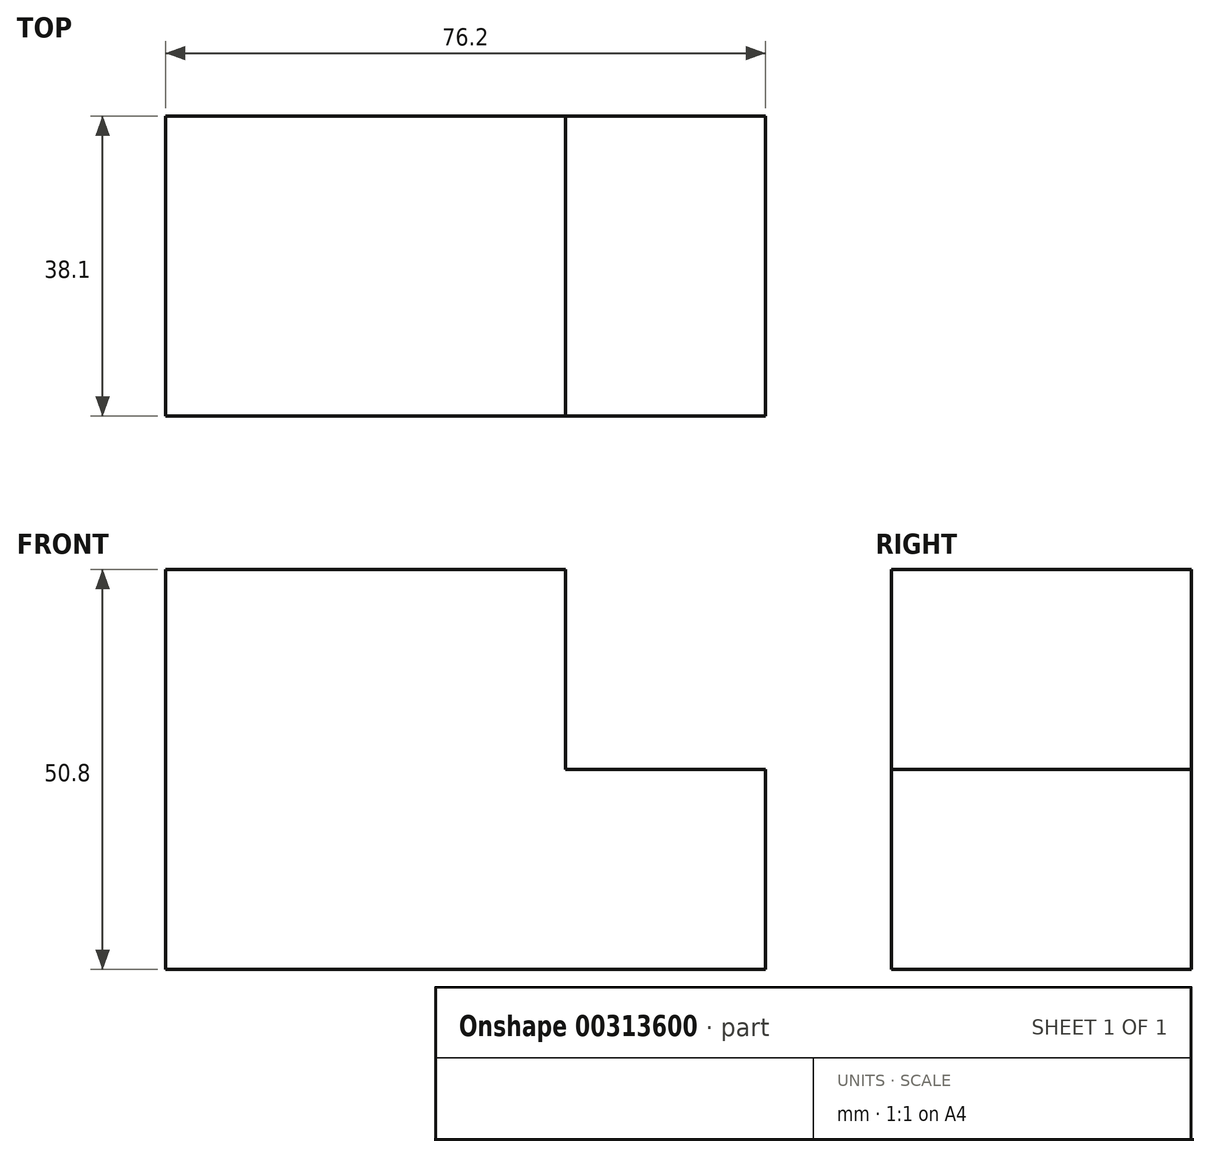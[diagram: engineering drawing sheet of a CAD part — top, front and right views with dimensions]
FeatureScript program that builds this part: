
annotation { "Feature Type Name" : "Feature", "Feature Type Description" : "" }
export const myFeature = defineFeature(function(context is Context, id is Id, definition is map)
    precondition{}
    {
        {
            var Q0;
            Q0=qCreatedBy(makeId("Front.planeOp"),FACE);
            var sketch = newSketch(context, id + "F0", { "sketchPlane" : qUnion([Q0])});
            skLineSegment(sketch, "E0", {"start": v(-38.24, -50.8) * mm, "end": v(37.96, -50.8) * mm});
            skLineSegment(sketch, "E1", {"start": v(37.96, -25.4) * mm, "end": v(12.56, -25.4) * mm});
            skLineSegment(sketch, "E2", {"start": v(12.56, -25.4) * mm, "end": v(12.56, 0) * mm});
            skLineSegment(sketch, "E3", {"start": v(12.56, 0) * mm, "end": v(-38.24, 0) * mm});
            skLineSegment(sketch, "E4", {"start": v(-38.24, 0) * mm, "end": v(-38.24, -50.8) * mm});
            skLineSegment(sketch, "E5", {"start": v(37.96, -25.4) * mm, "end": v(37.96, -50.8) * mm});
            skSolve(sketch);
        }
        {
            var Q0;
            Q0=makeQuery(id+"F0.imprint","IMPRINT",FACE,{"disambiguationData":[TD([[makeQuery(id+"F0.imprint","IMPRINT",EDGE,{"derivedFrom":sQuery(id+"F0.wireOp",EDGE,"E0")}),1.0]])]});
            extrude(context, id + "F1", {"entities" : qUnion([Q0]), "depth" : 38.1 * mm});
        }
    });
